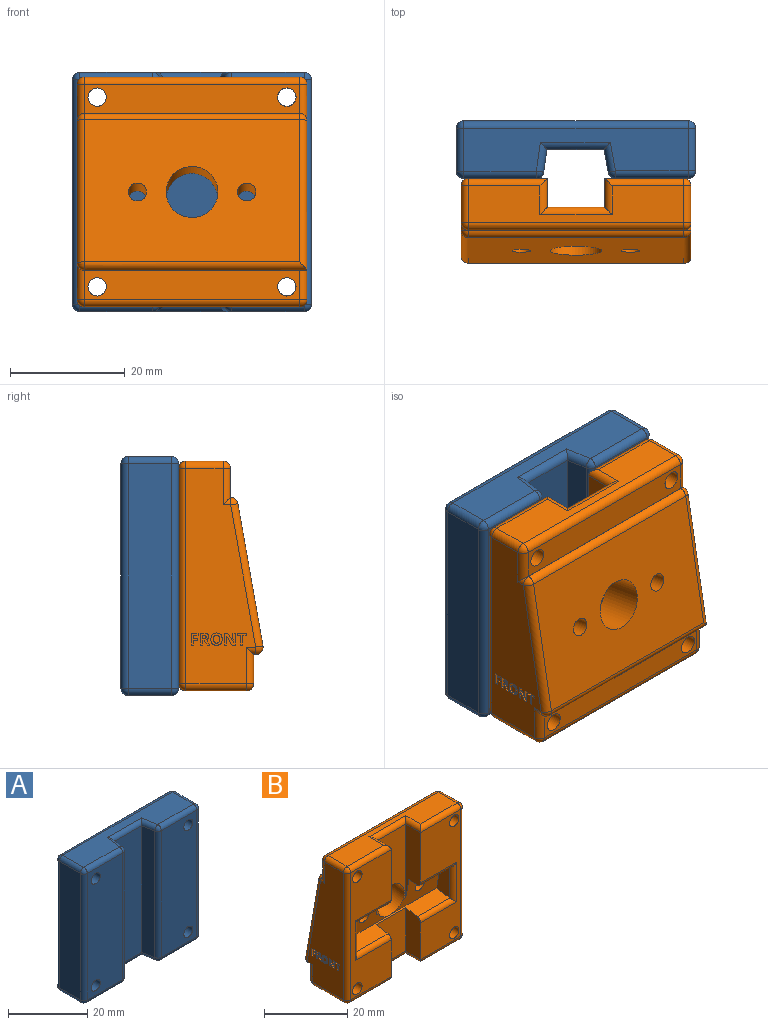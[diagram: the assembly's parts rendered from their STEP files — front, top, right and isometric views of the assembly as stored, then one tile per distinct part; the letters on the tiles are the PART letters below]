
ASSEMBLY  parts=2 mates=1
PART A: 48 faces, bbox 41.6x10x41.6 mm
  f0: plane 39.05x12.63mm, normal (0,-1,0), area 476.9mm2, adj f12,f13,f36,f41,f44,f47
  f1: plane 39.05x3.93mm, normal (0.99,-0.14,0), area 155.1mm2, adj f2,f42,f43,f47
  f2: plane 39.05x10mm, normal (0,-1,0), area 390.5mm2, adj f1,f3,f38,f39
  f3: plane 39.05x3.95mm, normal (-0.98,-0.17,0), area 156.6mm2, adj f2,f24,f33,f34
  f4: plane 39.05x12.66mm, normal (0,-1,0), area 478.4mm2, adj f10,f11,f15,f23,f24,f25
  f5: plane 39.05x7.46mm, normal (1,0,0), area 291.3mm2, adj f14,f15,f16,f17
  f6: plane 39.05x39.05mm, normal (0,1,0), area 1492.5mm2, adj f10,f11,f12,f13,f17,f22,f26,f27
  f7: plane 39.05x7.49mm, normal (-1,0,0), area 292.4mm2, adj f27,f32,f35,f36
  f8: plane 39.05x7.49mm, normal (0,0,1), area 226.8mm2, adj f14,f22,f23,f32,f33,f38,f41,f42
  f9: plane 39.05x7.49mm, normal (0,0,-1), area 226.8mm2, adj f16,f25,f26,f34,f35,f39,f43,f44
  f10: cylinder r=1.6mm len=10mm, axis (0,1,0), area 100.5mm2, adj f4,f6
  f11: cylinder r=1.6mm len=10mm, axis (0,1,0), area 100.5mm2, adj f4,f6
  f12: cylinder r=1.6mm len=10.03mm, axis (0,1,0), area 100.8mm2, adj f0,f6
  f13: cylinder r=1.6mm len=10.03mm, axis (0,1,0), area 100.8mm2, adj f0,f6
  f14: cylinder r=1.27mm len=7.46mm, axis (0,-1,0), area 14.9mm2, adj f5,f8,f18,f19
  f15: cylinder r=1.27mm len=39.05mm, axis (0,0,-1), area 77.9mm2, adj f4,f5,f19,f20
  f16: cylinder r=1.27mm len=7.46mm, axis (0,1,0), area 14.9mm2, adj f5,f9,f20,f21
  f17: cylinder r=1.27mm len=39.05mm, axis (0,0,1), area 77.9mm2, adj f5,f6,f18,f21
  f18: sphere r=1.27mm, area 2.5mm2, adj f14,f17,f22
  f19: sphere r=1.27mm, area 2.5mm2, adj f14,f15,f23
  f20: sphere r=1.27mm, area 2.5mm2, adj f15,f16,f25
  f21: sphere r=1.27mm, area 2.5mm2, adj f16,f17,f26
  f22: cylinder r=1.27mm len=39.05mm, axis (1,0,0), area 77.9mm2, adj f6,f8,f18,f28
  f23: cylinder r=1.27mm len=12.66mm, axis (-1,0,0), area 25.3mm2, adj f4,f8,f19,f29
  f24: cylinder r=1.27mm len=39.05mm, axis (0,0,-1), area 69.2mm2, adj f3,f4,f29,f30
  f25: cylinder r=1.27mm len=12.66mm, axis (1,0,0), area 25.3mm2, adj f4,f9,f20,f30
  f26: cylinder r=1.27mm len=39.05mm, axis (-1,0,0), area 77.9mm2, adj f6,f9,f21,f31
  f27: cylinder r=1.27mm len=39.05mm, axis (0,0,1), area 77.9mm2, adj f6,f7,f28,f31
  f28: sphere r=1.27mm, area 2.5mm2, adj f22,f27,f32
  f29: sphere r=1.27mm, area 2.3mm2, adj f23,f24,f33
  f30: sphere r=1.27mm, area 2.3mm2, adj f24,f25,f34
  f31: sphere r=1.27mm, area 2.5mm2, adj f26,f27,f35
  f32: cylinder r=1.27mm len=7.49mm, axis (0,1,0), area 14.9mm2, adj f7,f8,f28,f37
  f33: cylinder r=1.27mm len=5.22mm, axis (-0.17,0.98,0), area 8.8mm2, adj f3,f8,f29,f38
  f34: cylinder r=1.27mm len=5.22mm, axis (0.17,-0.98,0), area 8.8mm2, adj f3,f9,f30,f39
  f35: cylinder r=1.27mm len=7.49mm, axis (0,-1,0), area 14.9mm2, adj f7,f9,f31,f40
  f36: cylinder r=1.27mm len=39.05mm, axis (0,0,-1), area 77.9mm2, adj f0,f7,f37,f40
  f37: sphere r=1.27mm, area 2.5mm2, adj f32,f36,f41
  f38: cylinder r=1.27mm len=12.17mm, axis (-1,0,0), area 21.5mm2, adj f2,f8,f33,f42
  f39: cylinder r=1.27mm len=12.17mm, axis (1,0,0), area 21.5mm2, adj f2,f9,f34,f43
  f40: sphere r=1.27mm, area 2.5mm2, adj f35,f36,f44
  f41: cylinder r=1.27mm len=12.63mm, axis (-1,0,0), area 25.2mm2, adj f0,f8,f37,f45
  f42: cylinder r=1.27mm len=5.2mm, axis (-0.14,-0.99,0), area 8.7mm2, adj f1,f8,f38,f45
  f43: cylinder r=1.27mm len=5.2mm, axis (0.14,0.99,0), area 8.7mm2, adj f1,f9,f39,f46
  f44: cylinder r=1.27mm len=12.63mm, axis (1,0,0), area 25.2mm2, adj f0,f9,f40,f46
  f45: sphere r=1.27mm, area 2.3mm2, adj f41,f42,f47
  f46: sphere r=1.27mm, area 2.3mm2, adj f43,f44,f47
  f47: cylinder r=1.27mm len=39.05mm, axis (0,0,-1), area 71mm2, adj f0,f1,f45,f46
PART B: 221 faces, bbox 40x14.9x40 mm
  f0: plane 37.46x12.15mm, normal (1,0,0), area 343.5mm2, adj f103,f104,f105,f106,f107,f108,f109,f116
  f1: plane 37.46x12.37mm, normal (-1,0,0), area 345.7mm2, adj f18,f31,f32,f33,f34,f35,f36,f37
  f2: plane 16x8.86mm, normal (0,-0.98,-0.17), area 96.7mm2, adj f3,f4,f6,f7,f27,f28,f30
  f3: plane 32.04x4.45mm, normal (0,-0.17,0.98), area 104.5mm2, adj f2,f9,f10,f11,f25,f29,f30,f176
  f4: plane 11x2.45mm, normal (0,0.17,-0.98), area 27.3mm2, adj f2,f7,f30,f175
  f5: plane 21.7x5mm, normal (1,0,0), area 82.4mm2, adj f6,f8,f24,f25,f178,f184
  f6: plane 21.71x10.01mm, normal (0,-1,0), area 170.2mm2, adj f2,f5,f7,f25,f27,f181
  f7: plane 21.7x5mm, normal (-1,0,0), area 82.4mm2, adj f2,f4,f6,f12,f175,f182
  f8: plane 37.46x13.73mm, normal (0,-1,0), area 354.5mm2, adj f5,f9,f21,f23,f178,f179,f180,f188
  f9: plane 12.83x5mm, normal (1,0,0), area 61.7mm2, adj f3,f8,f10,f179,f193
  f10: plane 12.83x10mm, normal (0,-1,0), area 128.3mm2, adj f3,f9,f11,f189
  f11: plane 12.83x5mm, normal (-1,0,0), area 61.7mm2, adj f3,f10,f12,f176,f190
  f12: plane 37.46x13.73mm, normal (0,-1,0), area 354.5mm2, adj f7,f11,f20,f22,f175,f176,f177,f185
  f13: plane 37.46x5.08mm, normal (0,1,0), area 174.2mm2, adj f16,f22,f23,f183,f205,f217
  f14: plane 37.46x6.46mm, normal (0,0,1), area 179.3mm2, adj f181,f182,f183,f184,f185,f186,f187,f188
  f15: plane 37.46x10.51mm, normal (0,0,-1), area 331.1mm2, adj f189,f190,f193,f194,f197,f200,f201,f202
  f16: plane 37.46x0.05mm, normal (0,0,1), area 2mm2, adj f13,f207,f213,f216
  f17: plane 37.46x24.76mm, normal (0,0.98,0.17), area 862.4mm2, adj f26,f27,f28,f208,f209,f213,f214
  f18: plane 38.73x1.64mm, normal (0,0,-1), area 14.6mm2, adj f1,f19,f209,f210,f219
  f19: plane 37.46x5.08mm, normal (0,1,0), area 174.2mm2, adj f18,f20,f21,f202,f206,f219
  f20: cylinder r=1.6mm len=13.05mm, axis (0,-1,0), area 131.2mm2, adj f12,f19
  f21: cylinder r=1.6mm len=13.05mm, axis (0,-1,0), area 131.2mm2, adj f8,f19
  f22: cylinder r=1.6mm len=9mm, axis (0,-1,0), area 90.5mm2, adj f12,f13
  f23: cylinder r=1.6mm len=9mm, axis (0,-1,0), area 90.5mm2, adj f8,f13
  f24: plane 11x2.45mm, normal (0,0.17,-0.98), area 27.3mm2, adj f5,f25,f29,f178
  f25: plane 16x8.86mm, normal (0,-0.98,-0.17), area 96.7mm2, adj f3,f5,f6,f24,f26,f27,f29
  f26: cylinder r=1.59mm len=8.36mm, axis (0,0.98,0.17), area 79.1mm2, adj f17,f25
  f27: cylinder r=4.5mm len=10.24mm, axis (0,0.98,0.17), area 212.5mm2, adj f2,f6,f17,f25
  f28: cylinder r=1.59mm len=8.36mm, axis (0,0.98,0.17), area 79.1mm2, adj f2,f17
  f29: plane 9.61x4.23mm, normal (1,0,0), area 31.5mm2, adj f3,f24,f25,f178,f180
  f30: plane 9.61x4.23mm, normal (-1,0,0), area 31.5mm2, adj f2,f3,f4,f175,f177
  f31: extruded ~1.27x0.79mm, area 1.1mm2, adj f1,f32,f44,f45
  f32: extruded ~1.27x0.73mm, area 1mm2, adj f1,f31,f33,f45
  f33: extruded ~1.27x0.73mm, area 1mm2, adj f1,f32,f34,f45
  f34: extruded ~1.27x0.79mm, area 1.1mm2, adj f1,f33,f35,f45
  f35: extruded ~1.27x0.79mm, area 1.1mm2, adj f1,f34,f36,f45
  f36: extruded ~1.27x0.73mm, area 1mm2, adj f1,f35,f37,f45
  f37: extruded ~1.27x0.73mm, area 1mm2, adj f1,f36,f44,f45
  f38: extruded ~1.27x0.52mm, area 0.7mm2, adj f39,f43,f45,f46
  f39: extruded ~1.27x0.4mm, area 0.6mm2, adj f38,f40,f45,f46
  f40: extruded ~1.27x0.7mm, area 1.3mm2, adj f39,f41,f45,f46
  f41: extruded ~1.27x0.7mm, area 1.3mm2, adj f40,f42,f45,f46
  f42: extruded ~1.27x0.39mm, area 0.6mm2, adj f41,f43,f45,f46
  f43: extruded ~1.27x0.52mm, area 0.7mm2, adj f38,f42,f45,f46
  f44: extruded ~1.27x0.79mm, area 1.1mm2, adj f1,f31,f37,f45
  f45: plane 2.14x1.97mm, normal (-1,0,0), area 2.3mm2, adj f31,f32,f33,f34,f35,f36,f37,f38
  f46: plane 1.4x1.05mm, normal (-1,0,0), area 1.2mm2, adj f38,f39,f40,f41,f42,f43
  f47: plane 1.27x0.56mm, normal (0,1,0), area 0.7mm2, adj f48,f65,f66,f102
  f48: plane 1.27x0.13mm, normal (0,0,1), area 0.2mm2, adj f47,f49,f66,f102
  f49: extruded ~1.27x0.31mm, area 0.4mm2, adj f48,f50,f66,f102
  f50: extruded ~1.27x0.21mm, area 0.3mm2, adj f49,f51,f66,f102
  f51: extruded ~1.27x0.22mm, area 0.3mm2, adj f50,f52,f66,f102
  f52: extruded ~1.27x0.31mm, area 0.4mm2, adj f51,f65,f66,f102
  f53: plane 1.27x0.23mm, normal (0,0,1), area 0.3mm2, adj f1,f54,f64,f66
  f54: plane 1.27x0.8mm, normal (0,-0.85,0.53), area 1.2mm2, adj f1,f53,f55,f66
  f55: plane 1.27x0.49mm, normal (0,0,1), area 0.6mm2, adj f1,f54,f56,f66
  f56: extruded ~1.27x0.9mm, area 1.4mm2, adj f1,f55,f57,f66
  f57: extruded ~1.27x0.29mm, area 0.5mm2, adj f1,f56,f58,f66
  f58: extruded ~1.27x0.33mm, area 0.4mm2, adj f1,f57,f59,f66
  f59: extruded ~1.27x0.47mm, area 0.7mm2, adj f1,f58,f60,f66
  f60: extruded ~1.27x0.63mm, area 0.8mm2, adj f1,f59,f61,f66
  f61: plane 1.27x0.6mm, normal (0,0,-1), area 0.8mm2, adj f1,f60,f62,f66
  f62: plane 2.07x1.27mm, normal (0,-1,0), area 2.6mm2, adj f1,f61,f63,f66
  f63: plane 1.27x0.44mm, normal (0,0,1), area 0.6mm2, adj f1,f62,f64,f66
  f64: plane 1.27x0.8mm, normal (0,1,0), area 1mm2, adj f1,f53,f63,f66
  f65: plane 1.27x0.14mm, normal (0,0,-1), area 0.2mm2, adj f47,f52,f66,f102
  f66: plane 2.07x1.66mm, normal (-1,0,0), area 2.1mm2, adj f47,f48,f49,f50,f51,f52,f53,f54
  f67: plane 1.71x1.27mm, normal (0,1,0), area 2.2mm2, adj f1,f68,f74,f75
  f68: plane 1.27x0.56mm, normal (0,0,1), area 0.7mm2, adj f1,f67,f69,f75
  f69: plane 1.27x0.37mm, normal (0,1,0), area 0.5mm2, adj f1,f68,f70,f75
  f70: plane 1.57x1.27mm, normal (0,0,-1), area 2mm2, adj f1,f69,f71,f75
  f71: plane 1.27x0.37mm, normal (0,-1,0), area 0.5mm2, adj f1,f70,f72,f75
  f72: plane 1.27x0.56mm, normal (0,0,1), area 0.7mm2, adj f1,f71,f73,f75
  f73: plane 1.71x1.27mm, normal (0,-1,0), area 2.2mm2, adj f1,f72,f74,f75
  f74: plane 1.27x0.44mm, normal (0,0,1), area 0.6mm2, adj f1,f67,f73,f75
  f75: plane 2.07x1.57mm, normal (-1,0,0), area 1.3mm2, adj f67,f68,f69,f70,f71,f72,f73,f74
  f76: plane 2.07x1.27mm, normal (0,1,0), area 2.6mm2, adj f1,f77,f89,f90
  f77: plane 1.27x0.4mm, normal (0,0,-1), area 0.5mm2, adj f1,f76,f78,f90
  f78: plane 1.27x0.98mm, normal (0,-1,0), area 1.2mm2, adj f1,f77,f79,f90
  f79: extruded ~1.27x0.57mm, area 0.7mm2, adj f1,f78,f80,f90
  f80: plane 1.27x0.01mm, normal (0,0,-1), area 0mm2, adj f1,f79,f81,f90
  f81: plane 1.55x1.27mm, normal (0,0.87,-0.5), area 2.3mm2, adj f1,f80,f82,f90
  f82: plane 1.27x0.55mm, normal (0,0,-1), area 0.7mm2, adj f1,f81,f83,f90
  f83: plane 2.07x1.27mm, normal (0,-1,0), area 2.6mm2, adj f1,f82,f84,f90
  f84: plane 1.27x0.39mm, normal (0,0,1), area 0.5mm2, adj f1,f83,f85,f90
  f85: plane 1.27x0.98mm, normal (0,1,0), area 1.2mm2, adj f1,f84,f86,f90
  f86: extruded ~1.27x0.59mm, area 0.8mm2, adj f1,f85,f87,f90
  f87: plane 1.27x0.01mm, normal (0,0,1), area 0mm2, adj f1,f86,f88,f90
  f88: plane 1.57x1.27mm, normal (0,-0.87,0.5), area 2.3mm2, adj f1,f87,f89,f90
  f89: plane 1.27x0.56mm, normal (0,0,1), area 0.7mm2, adj f1,f76,f88,f90
  f90: plane 2.07x1.84mm, normal (-1,0,0), area 2.4mm2, adj f76,f77,f78,f79,f80,f81,f82,f83
  f91: plane 1.27x0.82mm, normal (0,1,0), area 1mm2, adj f1,f92,f100,f101
  f92: plane 1.27x0.7mm, normal (0,0,1), area 0.9mm2, adj f1,f91,f93,f101
  f93: plane 1.27x0.36mm, normal (0,1,0), area 0.5mm2, adj f1,f92,f94,f101
  f94: plane 1.27x0.7mm, normal (0,0,-1), area 0.9mm2, adj f1,f93,f95,f101
  f95: plane 1.27x0.53mm, normal (0,1,0), area 0.7mm2, adj f1,f94,f96,f101
  f96: plane 1.27x0.76mm, normal (0,0,1), area 1mm2, adj f1,f95,f97,f101
  f97: plane 1.27x0.36mm, normal (0,1,0), area 0.5mm2, adj f1,f96,f98,f101
  f98: plane 1.27x1.19mm, normal (0,0,-1), area 1.5mm2, adj f1,f97,f99,f101
  f99: plane 2.07x1.27mm, normal (0,-1,0), area 2.6mm2, adj f1,f98,f100,f101
  f100: plane 1.27x0.43mm, normal (0,0,1), area 0.5mm2, adj f1,f91,f99,f101
  f101: plane 2.07x1.19mm, normal (-1,0,0), area 1.4mm2, adj f91,f92,f93,f94,f95,f96,f97,f98
  f102: plane 0.56x0.55mm, normal (-1,0,0), area 0.3mm2, adj f47,f48,f49,f50,f51,f52,f65
  f103: extruded ~1.27x0.79mm, area 1.1mm2, adj f0,f104,f116,f117
  f104: extruded ~1.27x0.73mm, area 1mm2, adj f0,f103,f105,f117
  f105: extruded ~1.27x0.73mm, area 1mm2, adj f0,f104,f106,f117
  f106: extruded ~1.27x0.79mm, area 1.1mm2, adj f0,f105,f107,f117
  f107: extruded ~1.27x0.79mm, area 1.1mm2, adj f0,f106,f108,f117
  f108: extruded ~1.27x0.73mm, area 1mm2, adj f0,f107,f109,f117
  f109: extruded ~1.27x0.73mm, area 1mm2, adj f0,f108,f116,f117
  f110: extruded ~1.27x0.52mm, area 0.7mm2, adj f111,f115,f117,f118
  f111: extruded ~1.27x0.4mm, area 0.6mm2, adj f110,f112,f117,f118
  f112: extruded ~1.27x0.7mm, area 1.3mm2, adj f111,f113,f117,f118
  f113: extruded ~1.27x0.7mm, area 1.3mm2, adj f112,f114,f117,f118
  f114: extruded ~1.27x0.39mm, area 0.6mm2, adj f113,f115,f117,f118
  f115: extruded ~1.27x0.52mm, area 0.7mm2, adj f110,f114,f117,f118
  f116: extruded ~1.27x0.79mm, area 1.1mm2, adj f0,f103,f109,f117
  f117: plane 2.14x1.97mm, normal (1,0,0), area 2.3mm2, adj f103,f104,f105,f106,f107,f108,f109,f110
  f118: plane 1.4x1.05mm, normal (1,0,0), area 1.2mm2, adj f110,f111,f112,f113,f114,f115
  f119: plane 1.27x0.56mm, normal (0,-1,0), area 0.7mm2, adj f120,f137,f138,f174
  f120: plane 1.27x0.13mm, normal (0,0,1), area 0.2mm2, adj f119,f121,f138,f174
  f121: extruded ~1.27x0.31mm, area 0.4mm2, adj f120,f122,f138,f174
  f122: extruded ~1.27x0.21mm, area 0.3mm2, adj f121,f123,f138,f174
  f123: extruded ~1.27x0.22mm, area 0.3mm2, adj f122,f124,f138,f174
  f124: extruded ~1.27x0.31mm, area 0.4mm2, adj f123,f137,f138,f174
  f125: plane 1.27x0.23mm, normal (0,0,1), area 0.3mm2, adj f0,f126,f136,f138
  f126: plane 1.27x0.8mm, normal (0,0.85,0.53), area 1.2mm2, adj f0,f125,f127,f138
  f127: plane 1.27x0.49mm, normal (0,0,1), area 0.6mm2, adj f0,f126,f128,f138
  f128: extruded ~1.27x0.9mm, area 1.4mm2, adj f0,f127,f129,f138
  f129: extruded ~1.27x0.29mm, area 0.5mm2, adj f0,f128,f130,f138
  f130: extruded ~1.27x0.33mm, area 0.4mm2, adj f0,f129,f131,f138
  f131: extruded ~1.27x0.47mm, area 0.7mm2, adj f0,f130,f132,f138
  f132: extruded ~1.27x0.63mm, area 0.8mm2, adj f0,f131,f133,f138
  f133: plane 1.27x0.6mm, normal (0,0,-1), area 0.8mm2, adj f0,f132,f134,f138
  f134: plane 2.07x1.27mm, normal (0,1,0), area 2.6mm2, adj f0,f133,f135,f138
  f135: plane 1.27x0.44mm, normal (0,0,1), area 0.6mm2, adj f0,f134,f136,f138
  f136: plane 1.27x0.8mm, normal (0,-1,0), area 1mm2, adj f0,f125,f135,f138
  f137: plane 1.27x0.14mm, normal (0,0,-1), area 0.2mm2, adj f119,f124,f138,f174
  f138: plane 2.07x1.66mm, normal (1,0,0), area 2.1mm2, adj f119,f120,f121,f122,f123,f124,f125,f126
  f139: plane 1.71x1.27mm, normal (0,-1,0), area 2.2mm2, adj f0,f140,f146,f147
  f140: plane 1.27x0.56mm, normal (0,0,1), area 0.7mm2, adj f0,f139,f141,f147
  f141: plane 1.27x0.37mm, normal (0,-1,0), area 0.5mm2, adj f0,f140,f142,f147
  f142: plane 1.57x1.27mm, normal (0,0,-1), area 2mm2, adj f0,f141,f143,f147
  f143: plane 1.27x0.37mm, normal (0,1,0), area 0.5mm2, adj f0,f142,f144,f147
  f144: plane 1.27x0.56mm, normal (0,0,1), area 0.7mm2, adj f0,f143,f145,f147
  f145: plane 1.71x1.27mm, normal (0,1,0), area 2.2mm2, adj f0,f144,f146,f147
  f146: plane 1.27x0.44mm, normal (0,0,1), area 0.6mm2, adj f0,f139,f145,f147
  f147: plane 2.07x1.57mm, normal (1,0,0), area 1.3mm2, adj f139,f140,f141,f142,f143,f144,f145,f146
  f148: plane 2.07x1.27mm, normal (0,-1,0), area 2.6mm2, adj f0,f149,f161,f162
  f149: plane 1.27x0.4mm, normal (0,0,-1), area 0.5mm2, adj f0,f148,f150,f162
  f150: plane 1.27x0.98mm, normal (0,1,0), area 1.2mm2, adj f0,f149,f151,f162
  f151: extruded ~1.27x0.57mm, area 0.7mm2, adj f0,f150,f152,f162
  f152: plane 1.27x0.01mm, normal (0,0,-1), area 0mm2, adj f0,f151,f153,f162
  f153: plane 1.55x1.27mm, normal (0,-0.87,-0.5), area 2.3mm2, adj f0,f152,f154,f162
  f154: plane 1.27x0.55mm, normal (0,0,-1), area 0.7mm2, adj f0,f153,f155,f162
  f155: plane 2.07x1.27mm, normal (0,1,0), area 2.6mm2, adj f0,f154,f156,f162
  f156: plane 1.27x0.39mm, normal (0,0,1), area 0.5mm2, adj f0,f155,f157,f162
  f157: plane 1.27x0.98mm, normal (0,-1,0), area 1.2mm2, adj f0,f156,f158,f162
  f158: extruded ~1.27x0.59mm, area 0.8mm2, adj f0,f157,f159,f162
  f159: plane 1.27x0.01mm, normal (0,0,1), area 0mm2, adj f0,f158,f160,f162
  f160: plane 1.57x1.27mm, normal (0,0.87,0.5), area 2.3mm2, adj f0,f159,f161,f162
  f161: plane 1.27x0.56mm, normal (0,0,1), area 0.7mm2, adj f0,f148,f160,f162
  f162: plane 2.07x1.84mm, normal (1,0,0), area 2.4mm2, adj f148,f149,f150,f151,f152,f153,f154,f155
  f163: plane 1.27x0.82mm, normal (0,-1,0), area 1mm2, adj f0,f164,f172,f173
  f164: plane 1.27x0.7mm, normal (0,0,1), area 0.9mm2, adj f0,f163,f165,f173
  f165: plane 1.27x0.36mm, normal (0,-1,0), area 0.5mm2, adj f0,f164,f166,f173
  f166: plane 1.27x0.7mm, normal (0,0,-1), area 0.9mm2, adj f0,f165,f167,f173
  f167: plane 1.27x0.53mm, normal (0,-1,0), area 0.7mm2, adj f0,f166,f168,f173
  f168: plane 1.27x0.76mm, normal (0,0,1), area 1mm2, adj f0,f167,f169,f173
  f169: plane 1.27x0.36mm, normal (0,-1,0), area 0.5mm2, adj f0,f168,f170,f173
  f170: plane 1.27x1.19mm, normal (0,0,-1), area 1.5mm2, adj f0,f169,f171,f173
  f171: plane 2.07x1.27mm, normal (0,1,0), area 2.6mm2, adj f0,f170,f172,f173
  f172: plane 1.27x0.43mm, normal (0,0,1), area 0.5mm2, adj f0,f163,f171,f173
  f173: plane 2.07x1.19mm, normal (1,0,0), area 1.4mm2, adj f163,f164,f165,f166,f167,f168,f169,f170
  f174: plane 0.56x0.55mm, normal (1,0,0), area 0.3mm2, adj f119,f120,f121,f122,f123,f124,f137
  f175: cylinder r=1.27mm len=12.27mm, axis (-1,0,0), area 25.3mm2, adj f4,f7,f12,f30,f177
  f176: cylinder r=1.27mm len=12.27mm, axis (-1,0,0), area 20.4mm2, adj f3,f11,f12,f177
  f177: cylinder r=1.27mm len=11.72mm, axis (0,0,-1), area 20.1mm2, adj f3,f12,f30,f175,f176
  f178: cylinder r=1.27mm len=12.27mm, axis (-1,0,0), area 25.3mm2, adj f5,f8,f24,f29,f180
  f179: cylinder r=1.27mm len=12.27mm, axis (-1,0,0), area 20.4mm2, adj f3,f8,f9,f180
  f180: cylinder r=1.27mm len=11.72mm, axis (0,0,-1), area 20.1mm2, adj f3,f8,f29,f178,f179
  f181: cylinder r=1.27mm len=12.54mm, axis (-1,0,0), area 21.8mm2, adj f6,f14,f182,f184
  f182: cylinder r=1.27mm len=6.27mm, axis (0,1,0), area 10mm2, adj f7,f14,f181,f185
  f183: cylinder r=1.27mm len=37.46mm, axis (1,0,0), area 74.7mm2, adj f13,f14,f203,f218
  f184: cylinder r=1.27mm len=6.27mm, axis (0,-1,0), area 10mm2, adj f5,f14,f181,f188
  f185: cylinder r=1.27mm len=13.73mm, axis (-1,0,0), area 26.5mm2, adj f12,f14,f182,f191
  f186: cylinder r=1.27mm len=6.46mm, axis (0,-1,0), area 12.9mm2, adj f0,f14,f191,f218
  f187: cylinder r=1.27mm len=6.46mm, axis (0,1,0), area 12.9mm2, adj f1,f14,f192,f203
  f188: cylinder r=1.27mm len=13.73mm, axis (-1,0,0), area 26.5mm2, adj f8,f14,f184,f192
  f189: cylinder r=1.27mm len=12.54mm, axis (1,0,0), area 21.8mm2, adj f10,f15,f190,f193
  f190: cylinder r=1.27mm len=6.27mm, axis (0,-1,0), area 10mm2, adj f11,f15,f189,f194
  f191: sphere r=1.27mm, area 2.5mm2, adj f185,f186,f195
  f192: sphere r=1.27mm, area 2.5mm2, adj f187,f188,f196
  f193: cylinder r=1.27mm len=6.27mm, axis (0,1,0), area 10mm2, adj f9,f15,f189,f197
  f194: cylinder r=1.27mm len=13.73mm, axis (1,0,0), area 26.5mm2, adj f12,f15,f190,f198
  f195: cylinder r=1.27mm len=37.46mm, axis (0,0,-1), area 74.7mm2, adj f0,f12,f191,f198
  f196: cylinder r=1.27mm len=37.46mm, axis (0,0,-1), area 74.7mm2, adj f1,f8,f192,f199
  f197: cylinder r=1.27mm len=13.73mm, axis (1,0,0), area 26.5mm2, adj f8,f15,f193,f199
  f198: sphere r=1.27mm, area 2.5mm2, adj f194,f195,f200
  f199: sphere r=1.27mm, area 2.5mm2, adj f196,f197,f201
  f200: cylinder r=1.27mm len=10.51mm, axis (0,1,0), area 21mm2, adj f0,f15,f198,f204
  f201: cylinder r=1.27mm len=10.51mm, axis (0,-1,0), area 21mm2, adj f1,f15,f199,f220
  f202: cylinder r=1.27mm len=37.46mm, axis (-1,0,0), area 74.7mm2, adj f15,f19,f204,f220
  f203: sphere r=1.27mm, area 2.5mm2, adj f183,f187,f205
  f204: sphere r=1.27mm, area 2.5mm2, adj f200,f202,f206
  f205: cylinder r=1.27mm len=6.35mm, axis (0,0,-1), area 11.1mm2, adj f1,f13,f203,f207
  f206: cylinder r=1.27mm len=6.35mm, axis (0,0,1), area 11.1mm2, adj f0,f19,f204,f210
  f207: cylinder r=1.27mm len=1.32mm, axis (0,-1,0), area 1mm2, adj f1,f16,f205,f211
  f208: cylinder r=1.27mm len=26.23mm, axis (0,-0.17,0.98), area 51.8mm2, adj f1,f17,f209,f211
  f209: cylinder r=1.27mm len=38.73mm, axis (-1,0,0), area 84.9mm2, adj f1,f17,f18,f208,f212
  f210: cylinder r=1.27mm len=1.64mm, axis (0,1,0), area 1.7mm2, adj f0,f18,f206,f212
  f211: sphere r=1.27mm, area 2.3mm2, adj f207,f208,f213
  f212: sphere r=1.27mm, area 2.8mm2, adj f209,f210,f214
  f213: cylinder r=1.27mm len=37.46mm, axis (-1,0,0), area 66.4mm2, adj f16,f17,f211,f215
  f214: cylinder r=1.27mm len=24.98mm, axis (0,-0.17,0.98), area 50.2mm2, adj f0,f17,f212,f215
  f215: sphere r=1.27mm, area 2.3mm2, adj f213,f214,f216
  f216: cylinder r=1.27mm len=1.32mm, axis (0,-1,0), area 1mm2, adj f0,f16,f215,f217
  f217: cylinder r=1.27mm len=6.35mm, axis (0,0,-1), area 11.1mm2, adj f0,f13,f216,f218
  f218: sphere r=1.27mm, area 2.5mm2, adj f183,f186,f217
  f219: cylinder r=1.27mm len=5.08mm, axis (0,0,1), area 10.1mm2, adj f1,f18,f19,f220
  f220: sphere r=1.27mm, area 2.5mm2, adj f201,f202,f219
PLACE A t=(-8.04,13.28,6.08)mm
PLACE B rot(axis=(0,0,1),180deg) t=(-28.04,8.25,6.87)mm
MATE fastened B.f22 <-> A.f12  axis (0,1,0) through (-24.54,8.25,43.37)mm
